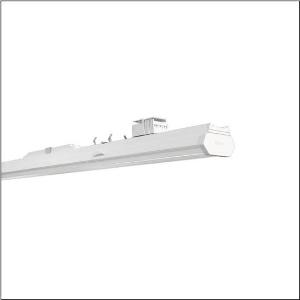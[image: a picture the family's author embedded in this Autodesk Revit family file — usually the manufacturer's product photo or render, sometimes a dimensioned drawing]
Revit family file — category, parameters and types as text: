
# Revit family: licross_11_protected_ho_51td12dn4fxm
name_source: partatom
category: Lighting Fixtures
units: mm (PartAtom-declared; Revit-internal decimal feet)

## family parameters
Cut with Voids When Loaded = No
Host = Face
Light Source = No
Part Type = Normal
Room Calculation Point = No
Round Connector Dimension = Use Diameter
Shared = No

## types (1)
- --- (1 x LED, 15270 lm, 87.3 W, 4000K)
    Apparent Load = 87 VA
    CIE Flux Codes = 70 91 97 98 100
    Color Rendering = 80
    Color Temperature = 4000K
    Default Elevation = 1800 mm
    Description = Licross 11 Protected HO, luminaire insert, of sheet steel, galvanised, coil coated, white, length: 1.500mm, width: 90mm, height: 101mm, LED rated luminous flux: 15.270lm, light colour: 840, SDCM (Standard Deviation of Colour Matching)MacAdam ≤ 2 SDCM (initial), control gear: DALI 2, with plug, 5-pole, with phase selection, mains connection: 220..240V, AC, 50/60Hz, rated input power: 87W, internal wiring halogen-free, primary optical cover: cover, of PMMA, light emission: direct distribution, primary light characteristic: symmetric, protection rating (complete): IP54, insulation class (complete): insulation class I (protective earthing), certification: CE, ENEC, VDE, UKCA, protection symbol: D if used in an environment with non-conductive dust loads with corresponding accessories, impact resistance: IK06, permissible ambient temperature for indoor applications: -25..+30°C, corresponds to IFS (International Featured Standards) requirements for safety and quality in the food industry, reducing of maximum allowable ambient temperature of 5°C with ceiling mounting, LABS conformity tested according to VDMA 24364:2018-05, The light source and the operating device comply with the requirements of the Ecodesign Regulation (EU) 2019/2020 and are replaceable in accordance with this regulation, packaging unit: 1 piece
    Height = 92 mm
    Lamp = 1 x LED
    Lamp Light Flux = 15270 lm
    Lamp Power = 87.3 W
    Lamp count = 1
    Length = 1500 mm
    Luminous efficacy = 175 lm/W
    Manufacturer = Siteco
    ModVariant = No
    Model = 51TD12DN4FXM
    Mounting Place = Ceiling
    Mounting Type = Pendant
    Number of Poles = 1
    OnlyDefault = Yes
    Power Factor = 1
    Product Name = Licross 11 Protected HO
    Product group = luminaire insert | ceiling pendant
    ProductGroupID = 901
    Protection Class = Protection class I
    Protection Degree = IP 54
    RLX_Detail_Level = 1
    RLX_Emergency_Light_Flux = 0 lm
    RLX_Emergency_Type = 0
    RLX_Emergency_Type_DB = No
    RlxData = <blob elided: 24633 chars, md5=63ef261a>
    Socket = socket
    Standby Power = 0 W
    System Light Flux = 15270 lm
    System Power = 87 W
    Type Comments = factory setting: luminous flux: 100 % | dim-lin: 254 | 589 mA
    Type Image = l_1256145.jpg
    URL = http://relux.com
    VarID = @adj_104323
    Voltage = 0 V
    Weight = 0.00 kg
    Width = 88 mm

## geometry (parser evidence)
native form markers: Blend x4, Sweep x12
no freeform markers — native parametric forms only
